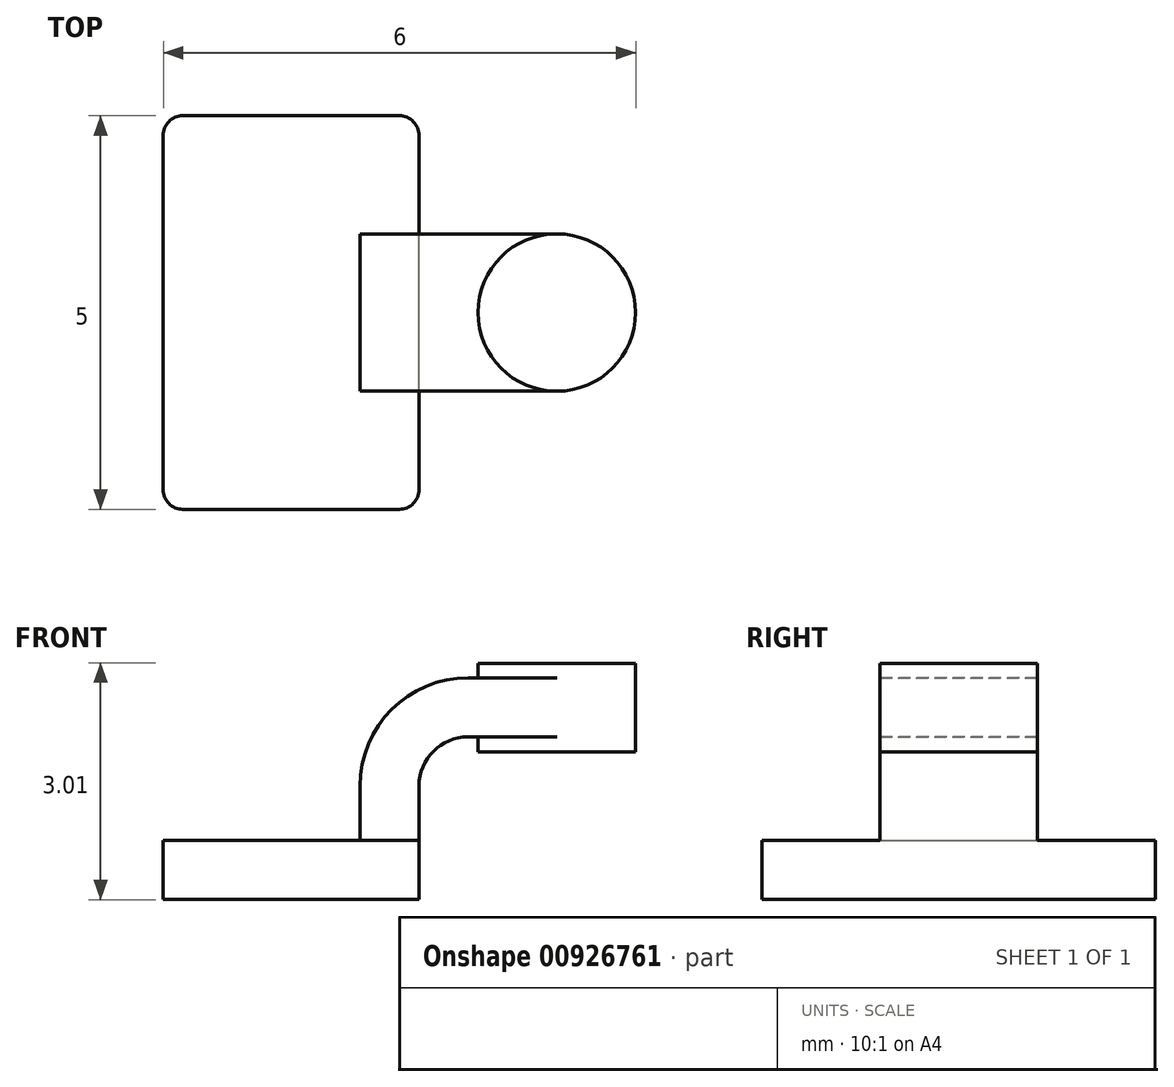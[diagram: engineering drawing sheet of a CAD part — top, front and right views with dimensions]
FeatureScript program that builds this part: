
annotation { "Feature Type Name" : "Feature", "Feature Type Description" : "" }
export const myFeature = defineFeature(function(context is Context, id is Id, definition is map)
    precondition{}
    {
        {
            var Q0;
            Q0=qCreatedBy(makeId("Front.planeOp"),FACE);
            var sketch = newSketch(context, id + "F0", { "sketchPlane" : qUnion([Q0])});
            skLineSegment(sketch, "E0.bottom", {"start": v(-1.63, -0.38) * mm, "end": v(1.63, -0.38) * mm});
            skLineSegment(sketch, "E0.top", {"start": v(-1.63, 0.38) * mm, "end": v(1.62, 0.38) * mm});
            skLineSegment(sketch, "E0.left", {"start": v(-1.62, -0.38) * mm, "end": v(-1.63, 0.38) * mm});
            skLineSegment(sketch, "E0.right", {"start": v(1.63, -0.38) * mm, "end": v(1.62, 0.38) * mm});
            skPoint(sketch, "E0.middle", {"position": v(0, 0) * mm});
            skLineSegment(sketch, "E1.bottom", {"start": v(2.37, 1.5) * mm, "end": v(4.37, 1.5) * mm});
            skLineSegment(sketch, "E1.top", {"start": v(2.37, 2.62) * mm, "end": v(4.37, 2.62) * mm});
            skLineSegment(sketch, "E1.left", {"start": v(2.37, 1.5) * mm, "end": v(2.37, 2.62) * mm});
            skLineSegment(sketch, "E1.right", {"start": v(4.37, 1.5) * mm, "end": v(4.37, 2.62) * mm});
            skPoint(sketch, "E1.middle", {"position": v(3.37, 2.06) * mm});
            skLineSegment(sketch, "E2", {"start": v(1.62, 0.37) * mm, "end": v(1.62, 1.07) * mm});
            skArc(sketch, "E3", {"start": v(1.62, 1.07) * mm, "mid": v(1.8, 1.5) * mm, "end": v(2.25, 1.7) * mm});
            skLineSegment(sketch, "E4", {"start": v(2.25, 1.7) * mm, "end": v(3.37, 1.7) * mm});
            skLineSegment(sketch, "E5.0", {"start": v(2.25, 2.44) * mm, "end": v(3.37, 2.44) * mm});
            skArc(sketch, "E5.1", {"start": v(0.87, 1.07) * mm, "mid": v(1.28, 2.04) * mm, "end": v(2.25, 2.44) * mm});
            skLineSegment(sketch, "E5.2", {"start": v(0.87, 0.37) * mm, "end": v(0.87, 1.07) * mm});
            skLineSegment(sketch, "E6", {"start": v(3.37, 2.62) * mm, "end": v(3.37, 1.5) * mm});
            skFitSpline(sketch, "E7", {"points": [v(-1.63, 0.38) * mm, v(2.25, 2.44) * mm], "startDerivative": vector(0.05, 4.06) * mm, "endDerivative": vector(5.24, 0.01) * mm});
            skCircle(sketch, "E8", {"center": v(-0.97, 0.92) * mm, "radius": 0.33 * mm});
            skCircle(sketch, "E9", {"center": v(-0.42, 1.55) * mm, "radius": 0.25 * mm});
            skCircle(sketch, "E10", {"center": v(0.03, 1.86) * mm, "radius": 0.15 * mm});
            skCircle(sketch, "E11", {"center": v(0.63, 2.14) * mm, "radius": 0.06 * mm});
            skCircle(sketch, "E12", {"center": v(0.37, 2.04) * mm, "radius": 0.1 * mm});
            skCircle(sketch, "E13", {"center": v(0.77, 2.2) * mm, "radius": 0.04 * mm});
            skSolve(sketch);
        }
        {
            var Q0;
            Q0=makeQuery(id+"F0.imprint","IMPRINT",FACE,{"disambiguationData":[TD([[makeQuery(id+"F0.imprint","IMPRINT",EDGE,{"derivedFrom":sQuery(id+"F0.wireOp",EDGE,"E0.bottom")}),1.0]])]});
            extrude(context, id + "F1", {"entities" : qUnion([Q0]), "endBound" : BoundingType.SYMMETRIC, "depth" : 5 * mm, "offsetDistance" : 25 * mm});
        }
        {
            var Q0;
            {var subQ0=sQuery(id+"F0.wireOp",EDGE,"E4");var subQ1=sQuery(id+"F0.wireOp",EDGE,"E1.left");var subQ2=makeQuery(id+"F0.imprint","INTERSECT",VERTEX,{"derivedFrom":[subQ1,subQ0]});Q0=makeQuery(id+"F0.imprint","IMPRINT",FACE,{"disambiguationData":[TD([[makeQuery(id+"F0.imprint","IMPRINT",EDGE,{"disambiguationData":[TD([[subQ2,-1.0]])],"derivedFrom":subQ1}),-1.0]])]});}
            var Q1;
            {var subQ1=sQuery(id+"F0.wireOp",EDGE,"E2");Q1=makeQuery(id+"F0.imprint","IMPRINT",FACE,{"disambiguationData":[TD([[makeQuery(id+"F0.imprint","IMPRINT",EDGE,{"derivedFrom":subQ1}),1.0]])]});}
            extrude(context, id + "F2", {"entities" : qUnion([Q0, Q1]), "operationType" : NewBodyOperationType.ADD, "endBound" : BoundingType.SYMMETRIC, "depth" : 2 * mm, "offsetDistance" : 25 * mm});
        }
        {
            var Q0;
            Q0=makeQuery(id+"F0.imprint","IMPRINT",FACE,{"disambiguationData":[TD([[makeQuery(id+"F0.imprint","IMPRINT",EDGE,{"derivedFrom":sQuery(id+"F0.wireOp",EDGE,"E5.1")}),1.0]])]});
            extrude(context, id + "F3", {"entities" : qUnion([Q0]), "operationType" : NewBodyOperationType.ADD, "endBound" : BoundingType.SYMMETRIC, "depth" : .625 * mm, "offsetDistance" : 25 * mm});
        }
        {
            var Q0;
            {var subQ0=sQuery(id+"F0.wireOp",EDGE,"E1.right");Q0=makeQuery(id+"F0.imprint","IMPRINT",FACE,{"disambiguationData":[TD([[makeQuery(id+"F0.imprint","IMPRINT",EDGE,{"derivedFrom":subQ0}),1.0]])]});}
            var Q1;
            Q1=sQuery(id+"F0.wireOp",EDGE,"E6");
            revolve(context, id + "F4", {"operationType" : NewBodyOperationType.ADD, "surfaceOperationType" : NewSurfaceOperationType.NEW, "entities" : qUnion([Q0]), "axis" : qUnion([Q1]), "revolveType" : RevolveType.FULL});
        }
        {
            var Q0;
            Q0=makeQuery(id+"F1.opExtrude","CAP_EDGE",EDGE,{"disambiguationData":[OSD([sQuery(id+"F0.wireOp",EDGE,"E0.right")])],"isStart":false});
            var Q1;
            Q1=makeQuery(id+"F1.opExtrude","CAP_EDGE",EDGE,{"disambiguationData":[OSD([sQuery(id+"F0.wireOp",EDGE,"E0.right")])],"isStart":true});
            var Q2;
            Q2=makeQuery(id+"F1.opExtrude","CAP_EDGE",EDGE,{"disambiguationData":[OSD([sQuery(id+"F0.wireOp",EDGE,"E0.left")])],"isStart":false});
            var Q3;
            Q3=makeQuery(id+"F1.opExtrude","CAP_EDGE",EDGE,{"disambiguationData":[OSD([sQuery(id+"F0.wireOp",EDGE,"E0.left")])],"isStart":true});
            fillet(context, id + "F5", {"entities" : qUnion([Q0, Q1, Q2, Q3]), "radius" : .25 * mm, "tangentPropagation" : true, "allowEdgeOverflow" : false});
        }
    });
